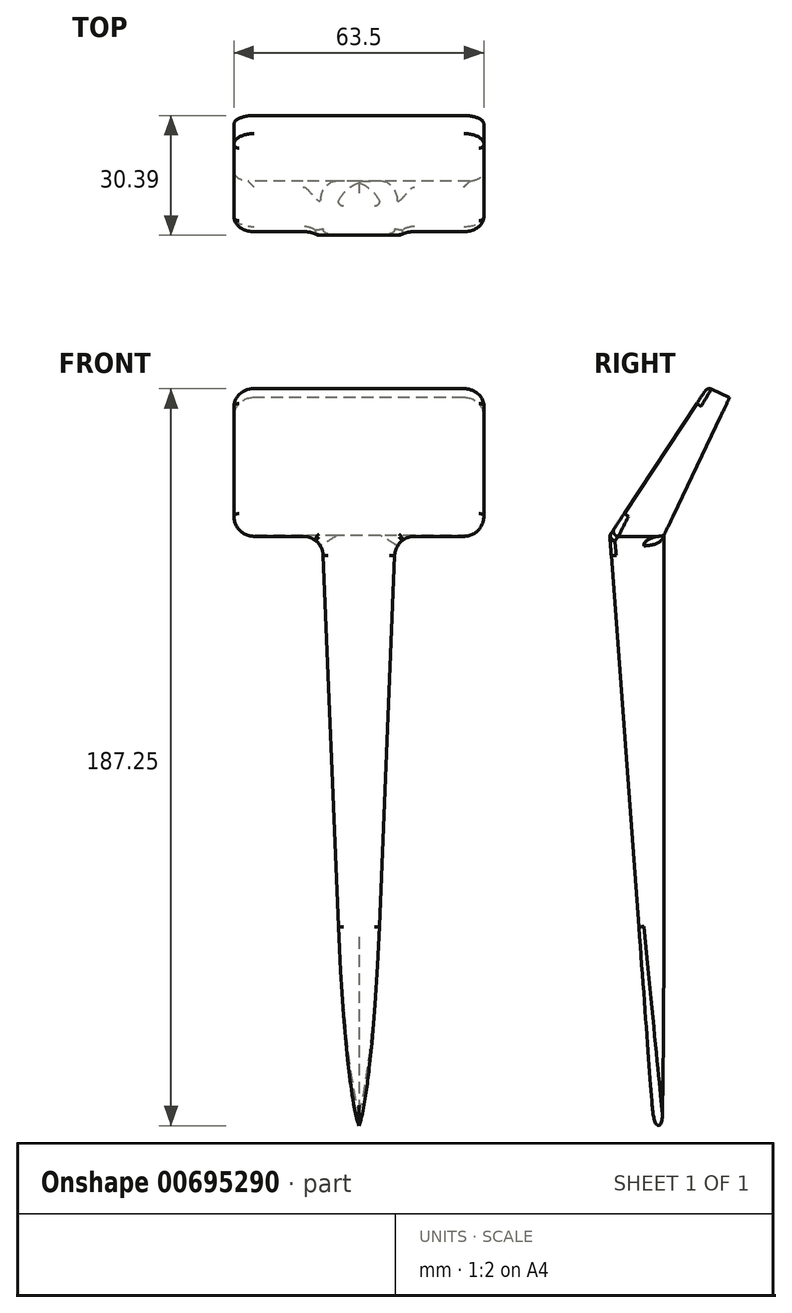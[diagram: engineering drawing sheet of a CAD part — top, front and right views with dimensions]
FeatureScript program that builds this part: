
annotation { "Feature Type Name" : "Feature", "Feature Type Description" : "" }
export const myFeature = defineFeature(function(context is Context, id is Id, definition is map)
    precondition{}
    {
        {
            var Q0;
            Q0=qCreatedBy(makeId("Front.planeOp"),FACE);
            var sketch = newSketch(context, id + "F0", { "sketchPlane" : qUnion([Q0])});
            skLineSegment(sketch, "E0", {"start": v(0, 203.2) * mm, "end": v(0, 0) * mm});
            skLineSegment(sketch, "E1.bottom", {"start": v(0, 203.2) * mm, "end": v(38.1, 203.2) * mm});
            skLineSegment(sketch, "E1.top", {"start": v(0, 165.1) * mm, "end": v(38.1, 165.1) * mm});
            skLineSegment(sketch, "E1.left", {"start": v(0, 203.2) * mm, "end": v(0, 165.1) * mm});
            skLineSegment(sketch, "E1.right", {"start": v(38.1, 203.2) * mm, "end": v(38.1, 165.1) * mm});
            skLineSegment(sketch, "E2", {"start": v(9.29, 165.1) * mm, "end": v(2.56, 0) * mm});
            skLineSegment(sketch, "E3", {"start": v(2.56, 0) * mm, "end": v(0, 0) * mm});
            skSolve(sketch);
        }
        {
            var Q0;
            Q0=qCreatedBy(makeId("Right.planeOp"),FACE);
            var sketch = newSketch(context, id + "F1", { "sketchPlane" : qUnion([Q0])});
            skLineSegment(sketch, "E4", {"start": v(-10.37, 175) * mm, "end": v(3.57, 169.22) * mm});
            skSolve(sketch);
        }
        {
            var Q0;
            Q0=qCreatedBy(makeId("Right.planeOp"),FACE);
            var sketch = newSketch(context, id + "F2", { "sketchPlane" : qUnion([Q0])});
            skLineSegment(sketch, "E5", {"start": v(34.86, 0) * mm, "end": v(34.86, 165.3) * mm});
            skLineSegment(sketch, "E6", {"start": v(34.86, 165.3) * mm, "end": v(51.54, 200.29) * mm});
            skLineSegment(sketch, "E7", {"start": v(51.54, 200.29) * mm, "end": v(45.97, 202.94) * mm});
            skLineSegment(sketch, "E8", {"start": v(45.97, 202.94) * mm, "end": v(21.12, 165.3) * mm});
            skLineSegment(sketch, "E9", {"start": v(21.12, 165.3) * mm, "end": v(33.4, 0) * mm});
            skLineSegment(sketch, "E10", {"start": v(33.4, 0) * mm, "end": v(34.86, 0) * mm});
            skSolve(sketch);
        }
        {
            var Q0;
            Q0=makeQuery(id+"F2.imprint","IMPRINT",FACE,{"disambiguationData":[TD([[makeQuery(id+"F2.imprint","IMPRINT",EDGE,{"derivedFrom":sQuery(id+"F2.wireOp",EDGE,"E5")}),1.0]])]});
            extrude(context, id + "F3", {"entities" : qUnion([Q0]), "endBound" : BoundingType.SYMMETRIC, "depth" : 63.5 * mm, "offsetDistance" : 25.4 * mm});
        }
        {
            var Q0;
            Q0=qCreatedBy(makeId("Front.planeOp"),FACE);
            var sketch = newSketch(context, id + "F4", { "sketchPlane" : qUnion([Q0])});
            skLineSegment(sketch, "E11", {"start": v(0, 0) * mm, "end": v(-2.47, 0) * mm});
            skLineSegment(sketch, "E12", {"start": v(-2.47, 0) * mm, "end": v(-9.28, 165.08) * mm});
            skLineSegment(sketch, "E13", {"start": v(-9.28, 165.08) * mm, "end": v(-36.76, 165.08) * mm});
            skLineSegment(sketch, "E14", {"start": v(-36.76, 165.08) * mm, "end": v(-36.76, 0) * mm});
            skLineSegment(sketch, "E15", {"start": v(-36.76, 0) * mm, "end": v(0, 0) * mm});
            skSolve(sketch);
        }
        {
            var Q0;
            {var subQ0=sQuery(id+"F4.wireOp",EDGE,"E12");Q0=makeQuery(id+"F4.imprint","IMPRINT",FACE,{"disambiguationData":[TD([[makeQuery(id+"F4.imprint","IMPRINT",EDGE,{"derivedFrom":subQ0}),1.0]])]});}
            extrude(context, id + "F5", {"entities" : qUnion([Q0]), "operationType" : NewBodyOperationType.REMOVE, "endBound" : BoundingType.SYMMETRIC, "oppositeDirection" : true, "depth" : 161.54 * mm, "offsetDistance" : 25.4 * mm});
        }
        {
            var Q0;
            Q0=qCreatedBy(makeId("Front.planeOp"),FACE);
            var sketch = newSketch(context, id + "F6", { "sketchPlane" : qUnion([Q0])});
            skLineSegment(sketch, "E16.bottom", {"start": v(115.05, -49.56) * mm, "end": v(0, -49.56) * mm});
            skLineSegment(sketch, "E16.top", {"start": v(115.05, 230.47) * mm, "end": v(0, 230.47) * mm});
            skLineSegment(sketch, "E16.left", {"start": v(115.05, -49.56) * mm, "end": v(115.05, 230.47) * mm});
            skLineSegment(sketch, "E16.right", {"start": v(0, -49.56) * mm, "end": v(0, 230.47) * mm});
            skSolve(sketch);
        }
        {
            var Q0;
            Q0=makeQuery(id+"F6.imprint","IMPRINT",FACE,{"disambiguationData":[TD([[makeQuery(id+"F6.imprint","IMPRINT",EDGE,{"derivedFrom":sQuery(id+"F6.wireOp",EDGE,"E16.bottom")}),-1.0]])]});
            extrude(context, id + "F7", {"entities" : qUnion([Q0]), "operationType" : NewBodyOperationType.REMOVE, "oppositeDirection" : true, "depth" : 80 * mm, "offsetDistance" : 25.4 * mm});
        }
        {
            var Q0;
            Q0=makeQuery(id+"F3.opExtrude","SWEPT_BODY",BODY,{"disambiguationData":[OSD([sQuery(id+"F2.wireOp",EDGE,"E5"),sQuery(id+"F2.wireOp",EDGE,"E6"),sQuery(id+"F2.wireOp",EDGE,"E7"),sQuery(id+"F2.wireOp",EDGE,"E8"),sQuery(id+"F2.wireOp",EDGE,"E9"),sQuery(id+"F2.wireOp",EDGE,"E10")])]});
            var Q1;
            Q1=makeQuery(id+"F7.boolean.opBoolean","COPY",FACE,{"derivedFrom":makeQuery(id+"F7.opExtrude","SWEPT_FACE",FACE,{"disambiguationData":[OSD([sQuery(id+"F6.wireOp",EDGE,"E16.right")])]})});
            mirror(context, id + "F8", {"operationType" : NewBodyOperationType.ADD, "entities" : qUnion([Q0]), "mirrorPlane" : qUnion([Q1])});
        }
        {
            var Q0;
            Q0=makeQuery(id+"F5.boolean.opBoolean","COPY",EDGE,{"derivedFrom":makeQuery(id+"F5.opExtrude","SWEPT_EDGE",EDGE,{"disambiguationData":[OSD([sQuery(id+"F4.wireOp",EDGE,"E12"),sQuery(id+"F4.wireOp",EDGE,"E13")])]})});
            var Q1;
            Q1=makeQuery(id+"F8.opPattern","COPY",EDGE,{"derivedFrom":makeQuery(id+"F5.boolean.opBoolean","COPY",EDGE,{"derivedFrom":makeQuery(id+"F5.opExtrude","SWEPT_EDGE",EDGE,{"disambiguationData":[OSD([sQuery(id+"F4.wireOp",EDGE,"E12"),sQuery(id+"F4.wireOp",EDGE,"E13")])]})}),"instanceName":"1"});
            var Q2;
            Q2=makeQuery(id+"F8.opPattern","COPY",EDGE,{"derivedFrom":makeQuery(id+"F5.boolean.opBoolean","INTERSECT",EDGE,{"derivedFrom":[makeQuery(id+"F3.opExtrude","CAP_FACE",FACE,{"disambiguationData":[OSD([sQuery(id+"F2.wireOp",EDGE,"E5"),sQuery(id+"F2.wireOp",EDGE,"E6"),sQuery(id+"F2.wireOp",EDGE,"E7"),sQuery(id+"F2.wireOp",EDGE,"E8"),sQuery(id+"F2.wireOp",EDGE,"E9"),sQuery(id+"F2.wireOp",EDGE,"E10")])],"isStart":true}),makeQuery(id+"F5.opExtrude","SWEPT_FACE",FACE,{"disambiguationData":[OSD([sQuery(id+"F4.wireOp",EDGE,"E13")])]})]}),"instanceName":"1"});
            var Q3;
            Q3=makeQuery(id+"F5.boolean.opBoolean","INTERSECT",EDGE,{"derivedFrom":[makeQuery(id+"F3.opExtrude","CAP_FACE",FACE,{"disambiguationData":[OSD([sQuery(id+"F2.wireOp",EDGE,"E5"),sQuery(id+"F2.wireOp",EDGE,"E6"),sQuery(id+"F2.wireOp",EDGE,"E7"),sQuery(id+"F2.wireOp",EDGE,"E8"),sQuery(id+"F2.wireOp",EDGE,"E9"),sQuery(id+"F2.wireOp",EDGE,"E10")])],"isStart":true}),makeQuery(id+"F5.opExtrude","SWEPT_FACE",FACE,{"disambiguationData":[OSD([sQuery(id+"F4.wireOp",EDGE,"E13")])]})]});
            fillet(context, id + "F9", {"entities" : qUnion([Q0, Q1, Q2, Q3]), "radius" : 5.08 * mm, "tangentPropagation" : true, "allowEdgeOverflow" : false});
        }
        {
            var Q0;
            Q0=makeQuery(id+"F3.opExtrude","CAP_EDGE",EDGE,{"disambiguationData":[OSD([sQuery(id+"F2.wireOp",EDGE,"E7")])],"isStart":true});
            var Q1;
            Q1=makeQuery(id+"F8.opPattern","COPY",EDGE,{"derivedFrom":makeQuery(id+"F3.opExtrude","CAP_EDGE",EDGE,{"disambiguationData":[OSD([sQuery(id+"F2.wireOp",EDGE,"E7")])],"isStart":true}),"instanceName":"1"});
            fillet(context, id + "F10", {"entities" : qUnion([Q0, Q1]), "radius" : 5.08 * mm, "tangentPropagation" : true, "allowEdgeOverflow" : false});
        }
        {
            var Q0;
            Q0=makeQuery(id+"F3.opExtrude","CAP_EDGE",EDGE,{"disambiguationData":[OSD([sQuery(id+"F2.wireOp",EDGE,"E8")])],"isStart":true});
            fillet(context, id + "F11", {"entities" : qUnion([Q0]), "radius" : 1.27 * mm, "tangentPropagation" : true, "allowEdgeOverflow" : false});
        }
        {
            var Q0;
            Q0=makeQuery(id+"F8.opPattern","COPY",EDGE,{"derivedFrom":makeQuery(id+"F5.boolean.opBoolean","INTERSECT",EDGE,{"derivedFrom":[makeQuery(id+"F3.opExtrude","SWEPT_FACE",FACE,{"disambiguationData":[OSD([sQuery(id+"F2.wireOp",EDGE,"E5")])]}),makeQuery(id+"F5.opExtrude","SWEPT_FACE",FACE,{"disambiguationData":[OSD([sQuery(id+"F4.wireOp",EDGE,"E12")])]})]}),"instanceName":"1"});
            var Q1;
            Q1=makeQuery(id+"F5.boolean.opBoolean","INTERSECT",EDGE,{"derivedFrom":[makeQuery(id+"F3.opExtrude","SWEPT_FACE",FACE,{"disambiguationData":[OSD([sQuery(id+"F2.wireOp",EDGE,"E5")])]}),makeQuery(id+"F5.opExtrude","SWEPT_FACE",FACE,{"disambiguationData":[OSD([sQuery(id+"F4.wireOp",EDGE,"E12")])]})]});
            fillet(context, id + "F12", {"entities" : qUnion([Q0, Q1]), "radius" : 5.08 * mm, "tangentPropagation" : true, "allowEdgeOverflow" : false});
        }
        {
            var Q0;
            {var subQ0=makeQuery(id+"F3.opExtrude","SWEPT_FACE",FACE,{"disambiguationData":[OSD([sQuery(id+"F2.wireOp",EDGE,"E9")])]});Q0=makeQuery(id+"F12.opFillet","BLEND_EDGE",EDGE,{"blendedFrom":[makeQuery(id+"F5.boolean.opBoolean","INTERSECT",EDGE,{"derivedFrom":[makeQuery(id+"F3.opExtrude","SWEPT_FACE",FACE,{"disambiguationData":[OSD([sQuery(id+"F2.wireOp",EDGE,"E5")])]}),makeQuery(id+"F5.opExtrude","SWEPT_FACE",FACE,{"disambiguationData":[OSD([sQuery(id+"F4.wireOp",EDGE,"E12")])]})]}),makeQuery(id+"F8.boolean.opBoolean","MERGE",FACE,{"derivedFrom":[subQ0,makeQuery(id+"F8.opPattern","COPY",FACE,{"derivedFrom":subQ0,"instanceName":"1"})]})],"blendedInto":[makeQuery(id+"F8.boolean.opBoolean","MERGE",FACE,{"derivedFrom":[subQ0,makeQuery(id+"F8.opPattern","COPY",FACE,{"derivedFrom":subQ0,"instanceName":"1"})]})]});}
            fillet(context, id + "F13", {"entities" : qUnion([Q0]), "radius" : 1.27 * mm, "tangentPropagation" : true, "allowEdgeOverflow" : false});
        }
    });
